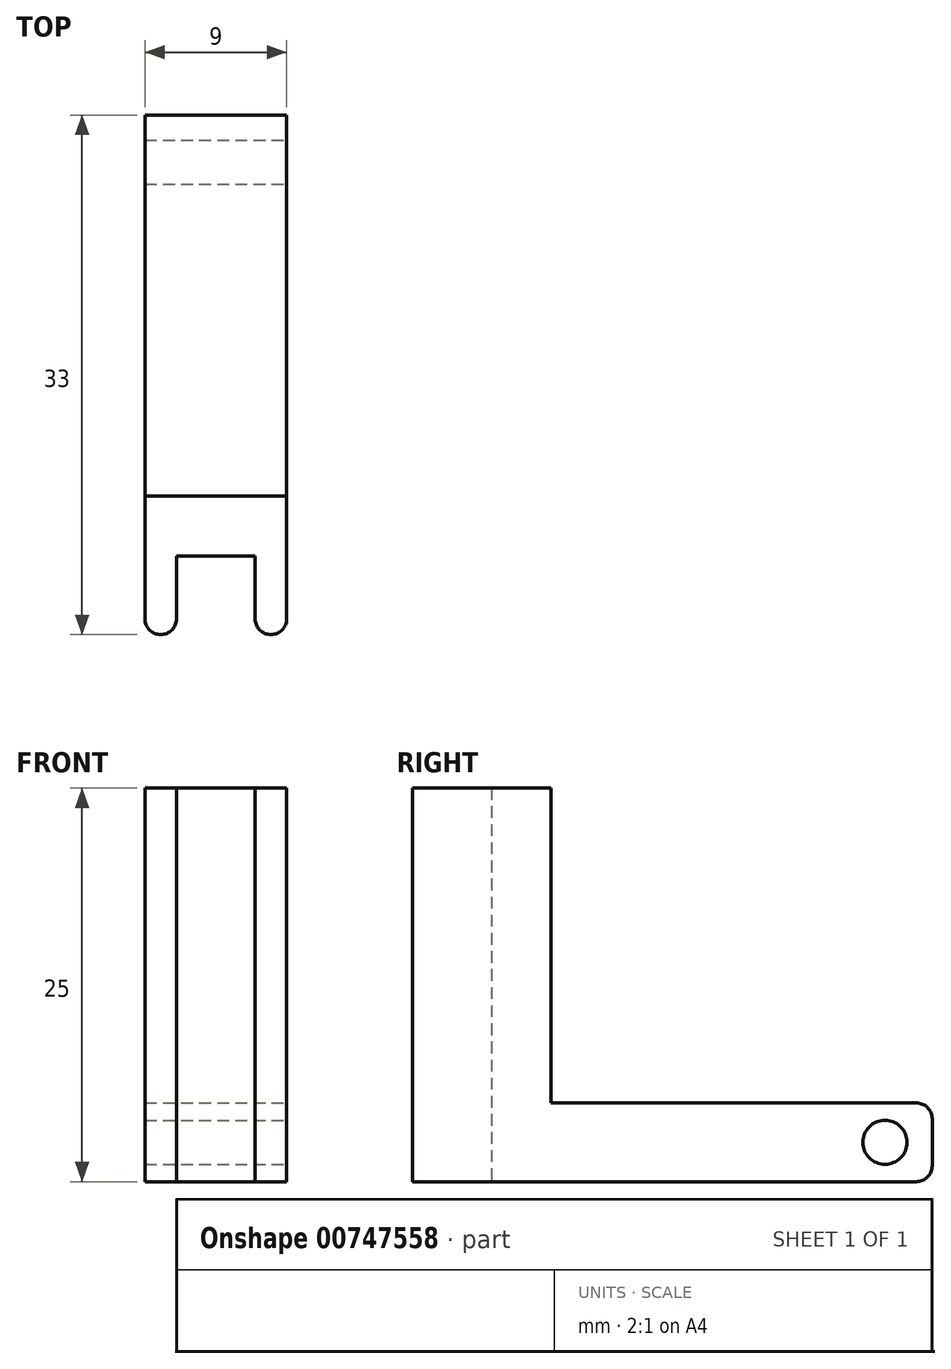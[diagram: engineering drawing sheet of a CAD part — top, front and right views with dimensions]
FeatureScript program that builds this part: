
annotation { "Feature Type Name" : "Feature", "Feature Type Description" : "" }
export const myFeature = defineFeature(function(context is Context, id is Id, definition is map)
    precondition{}
    {
        {
            var Q0;
            Q0=qCreatedBy(makeId("Top.planeOp"),FACE);
            var sketch = newSketch(context, id + "F0", { "sketchPlane" : qUnion([Q0])});
            skLineSegment(sketch, "E0.bottom", {"start": v(-4.5, 0) * mm, "end": v(4.5, 0) * mm});
            skLineSegment(sketch, "E0.top", {"start": v(-4.5, 33) * mm, "end": v(4.5, 33) * mm});
            skLineSegment(sketch, "E0.left", {"start": v(-4.5, 0) * mm, "end": v(-4.5, 33) * mm});
            skLineSegment(sketch, "E0.right", {"start": v(4.5, 0) * mm, "end": v(4.5, 33) * mm});
            skLineSegment(sketch, "E1.bottom", {"start": v(-2.5, 0) * mm, "end": v(2.5, 0) * mm});
            skLineSegment(sketch, "E1.top", {"start": v(-2.5, 5) * mm, "end": v(2.5, 5) * mm});
            skLineSegment(sketch, "E1.left", {"start": v(-2.5, 0) * mm, "end": v(-2.5, 5) * mm});
            skLineSegment(sketch, "E1.right", {"start": v(2.5, 0) * mm, "end": v(2.5, 5) * mm});
            skLineSegment(sketch, "E2", {"start": v(-4.5, 8.8) * mm, "end": v(4.5, 8.8) * mm});
            skSolve(sketch);
        }
        {
            var Q0;
            Q0=makeQuery(id+"F0.imprint","IMPRINT",FACE,{"disambiguationData":[TD([[makeQuery(id+"F0.imprint","IMPRINT",EDGE,{"derivedFrom":sQuery(id+"F0.wireOp",EDGE,"E1.top")}),1.0]])]});
            extrude(context, id + "F1", {"entities" : qUnion([Q0]), "depth" : 25 * mm, "offsetDistance" : 25 * mm});
        }
        {
            var Q0;
            {var subQ0=sQuery(id+"F0.wireOp",EDGE,"E0.top");Q0=makeQuery(id+"F0.imprint","IMPRINT",FACE,{"disambiguationData":[TD([[makeQuery(id+"F0.imprint","IMPRINT",EDGE,{"derivedFrom":subQ0}),-1.0]])]});}
            extrude(context, id + "F2", {"entities" : qUnion([Q0]), "operationType" : NewBodyOperationType.ADD, "depth" : 5 * mm, "offsetDistance" : 25 * mm});
        }
        {
            var Q0;
            Q0=qCreatedBy(makeId("Right.planeOp"),FACE);
            var sketch = newSketch(context, id + "F3", { "sketchPlane" : qUnion([Q0])});
            skCircle(sketch, "E3", {"center": v(30, 2.5) * mm, "radius": 1.4 * mm});
            skSolve(sketch);
        }
        {
            var Q0;
            Q0 = qSketchRegion(id + "F3", true);
            extrude(context, id + "F4", {"entities" : qUnion([Q0]), "operationType" : NewBodyOperationType.REMOVE, "endBound" : BoundingType.SYMMETRIC, "oppositeDirection" : true, "depth" : 25 * mm, "offsetDistance" : 25 * mm});
        }
        {
            var Q0;
            Q0=makeQuery(id+"F2.opExtrude","CAP_EDGE",EDGE,{"disambiguationData":[OSD([sQuery(id+"F0.wireOp",EDGE,"E0.top")])],"isStart":false});
            var Q1;
            Q1=makeQuery(id+"F2.opExtrude","CAP_EDGE",EDGE,{"disambiguationData":[OSD([sQuery(id+"F0.wireOp",EDGE,"E0.top")])],"isStart":true});
            var Q2;
            Q2=makeQuery(id+"F1.opExtrude","SWEPT_EDGE",EDGE,{"disambiguationData":[OSD([sQuery(id+"F0.wireOp",EDGE,"E0.bottom"),sQuery(id+"F0.wireOp",EDGE,"E1.bottom"),sQuery(id+"F0.wireOp",EDGE,"E1.left")])]});
            var Q3;
            Q3=makeQuery(id+"F1.opExtrude","SWEPT_EDGE",EDGE,{"disambiguationData":[OSD([sQuery(id+"F0.wireOp",EDGE,"E0.bottom"),sQuery(id+"F0.wireOp",EDGE,"E1.bottom"),sQuery(id+"F0.wireOp",EDGE,"E1.right")])]});
            var Q4;
            Q4=makeQuery(id+"F1.opExtrude","SWEPT_EDGE",EDGE,{"disambiguationData":[OSD([sQuery(id+"F0.wireOp",EDGE,"E0.bottom"),sQuery(id+"F0.wireOp",EDGE,"E0.left")])]});
            var Q5;
            Q5=makeQuery(id+"F1.opExtrude","SWEPT_EDGE",EDGE,{"disambiguationData":[OSD([sQuery(id+"F0.wireOp",EDGE,"E0.bottom"),sQuery(id+"F0.wireOp",EDGE,"E0.right")])]});
            fillet(context, id + "F5", {"entities" : qUnion([Q0, Q1, Q2, Q3, Q4, Q5]), "radius" : 1 * mm, "tangentPropagation" : true, "allowEdgeOverflow" : false});
        }
    });
